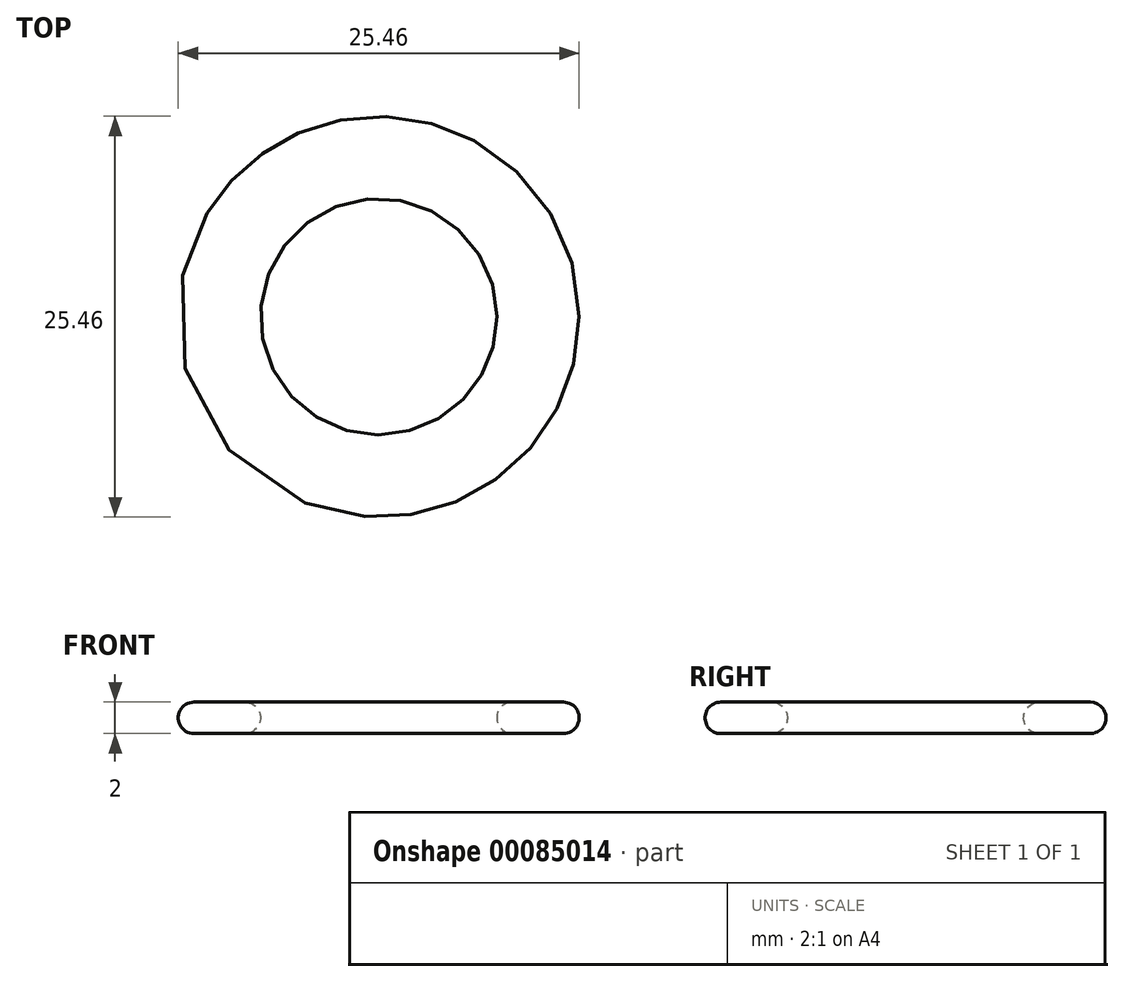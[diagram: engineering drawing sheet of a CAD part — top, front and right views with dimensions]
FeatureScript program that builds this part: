
annotation { "Feature Type Name" : "Feature", "Feature Type Description" : "" }
export const myFeature = defineFeature(function(context is Context, id is Id, definition is map)
    precondition{}
    {
        {
            var Q0;
            Q0=qCreatedBy(makeId("Top.planeOp"),FACE);
            var sketch = newSketch(context, id + "F0", { "sketchPlane" : qUnion([Q0])});
            skCircle(sketch, "E0", {"center": v(0, 0) * mm, "radius": 7.5 * mm});
            skCircle(sketch, "E1", {"center": v(0, 0) * mm, "radius": 12.73 * mm});
            skSolve(sketch);
        }
        {
            var Q0;
            Q0=makeQuery(id+"F0.imprint","IMPRINT",FACE,{"disambiguationData":[TD([[makeQuery(id+"F0.imprint","IMPRINT",EDGE,{"derivedFrom":sQuery(id+"F0.wireOp",EDGE,"E0")}),-1.0]])]});
            extrude(context, id + "F1", {"entities" : qUnion([Q0]), "depth" : 2 * mm});
        }
        {
            var Q0;
            Q0=makeQuery(id+"F1.opExtrude","SWEPT_FACE",FACE,{"disambiguationData":[OSD([sQuery(id+"F0.wireOp",EDGE,"E1")])]});
            fillet(context, id + "F2", {"entities" : qUnion([Q0]), "radius" : 1 * mm, "tangentPropagation" : true, "allowEdgeOverflow" : false});
        }
        {
            var Q0;
            Q0=makeQuery(id+"F1.opExtrude","SWEPT_FACE",FACE,{"disambiguationData":[OSD([sQuery(id+"F0.wireOp",EDGE,"E0")])]});
            fillet(context, id + "F3", {"entities" : qUnion([Q0]), "radius" : 1 * mm, "tangentPropagation" : true, "allowEdgeOverflow" : false});
        }
    });
